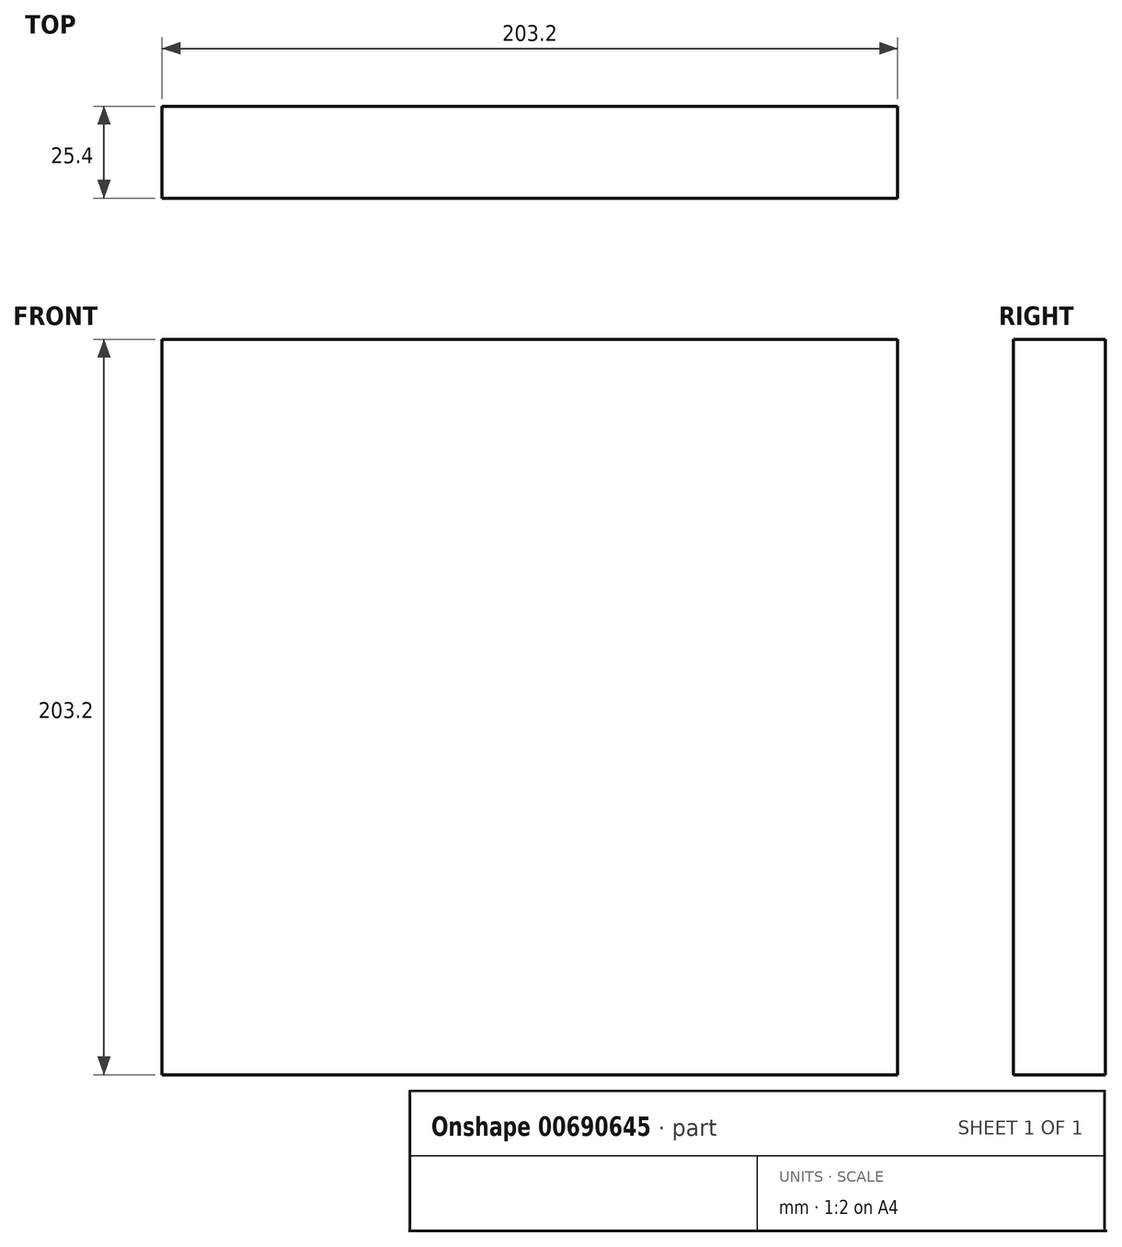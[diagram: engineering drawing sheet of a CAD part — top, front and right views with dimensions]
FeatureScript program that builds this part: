
annotation { "Feature Type Name" : "Feature", "Feature Type Description" : "" }
export const myFeature = defineFeature(function(context is Context, id is Id, definition is map)
    precondition{}
    {
        {
            var Q0;
            Q0=qCreatedBy(makeId("Front.planeOp"),FACE);
            var sketch = newSketch(context, id + "F0", { "sketchPlane" : qUnion([Q0])});
            skLineSegment(sketch, "E0.bottom", {"start": v(-96.73, 137.93) * mm, "end": v(106.47, 137.93) * mm});
            skLineSegment(sketch, "E0.top", {"start": v(-96.73, -65.27) * mm, "end": v(106.47, -65.27) * mm});
            skLineSegment(sketch, "E0.left", {"start": v(-96.73, 137.93) * mm, "end": v(-96.73, -65.27) * mm});
            skLineSegment(sketch, "E0.right", {"start": v(106.47, 137.93) * mm, "end": v(106.47, -65.27) * mm});
            skSolve(sketch);
        }
        {
            var Q0;
            Q0=makeQuery(id+"F0.imprint","IMPRINT",FACE,{"disambiguationData":[TD([[makeQuery(id+"F0.imprint","IMPRINT",EDGE,{"derivedFrom":sQuery(id+"F0.wireOp",EDGE,"E0.bottom")}),-1.0]])]});
            extrude(context, id + "F1", {"entities" : qUnion([Q0]), "depth" : 25.4 * mm, "offsetDistance" : 25.4 * mm});
        }
    });
